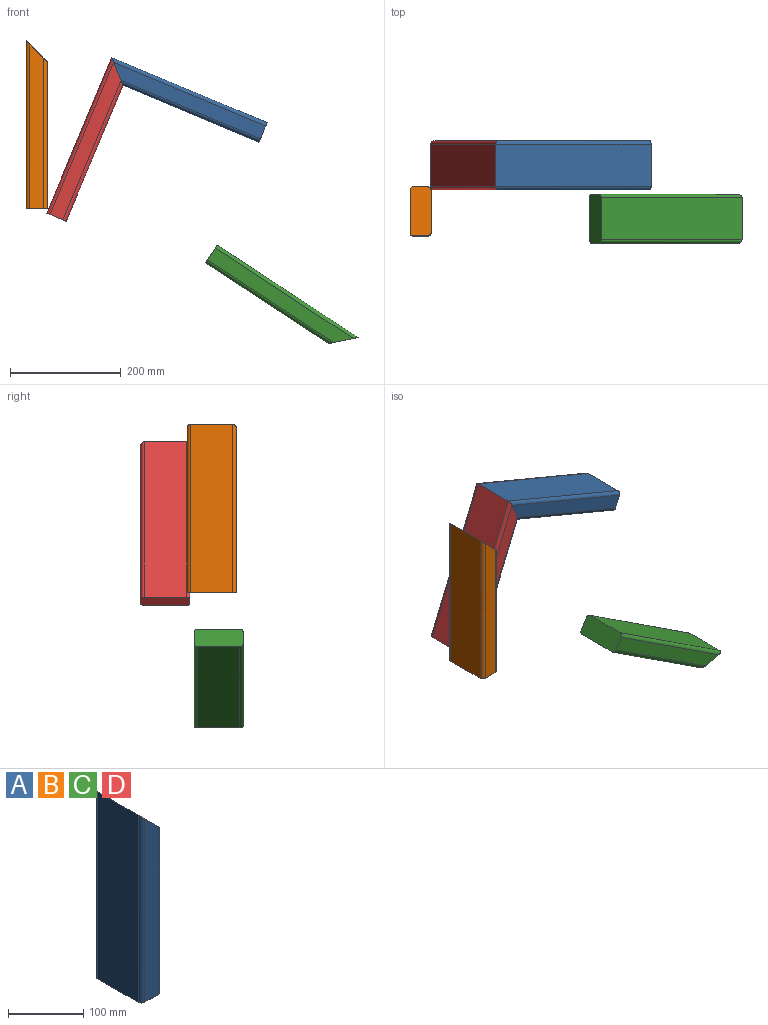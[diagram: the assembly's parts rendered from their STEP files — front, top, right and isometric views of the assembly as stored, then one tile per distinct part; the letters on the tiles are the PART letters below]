
ASSEMBLY  parts=4 mates=1
PART A: 10 faces, bbox 38.1x88.9x304.8 mm
  f0: plane 298.45x25.4mm, normal (0,-1,0), area 7258.1mm2, adj f1,f6,f8,f9
  f1: cylinder r=6.35mm len=273.05mm, axis (0,0,-1), area 2683.2mm2, adj f0,f2,f8,f9
  f2: plane 266.7x76.2mm, normal (1,0,0), area 20322.5mm2, adj f1,f3,f8,f9
  f3: cylinder r=6.35mm len=273.05mm, axis (0,0,-1), area 2683.2mm2, adj f2,f4,f8,f9
  f4: plane 298.45x25.4mm, normal (0,1,0), area 7258.1mm2, adj f3,f5,f8,f9
  f5: cylinder r=6.35mm len=304.8mm, axis (0,0,-1), area 3017.2mm2, adj f4,f7,f8,f9
  f6: cylinder r=6.35mm len=304.8mm, axis (0,0,-1), area 3017.2mm2, adj f0,f7,f8,f9
  f7: plane 304.8x76.2mm, normal (-1,0,0), area 23225.8mm2, adj f5,f6,f8,f9
  f8: plane 88.9x38.1mm, normal (0,0,-1), area 3352.5mm2, adj f0,f1,f2,f3,f4,f5,f6,f7
  f9: plane 88.9x38.1mm, normal (0.71,0,0.71), area 4741.1mm2, adj f0,f1,f2,f3,f4,f5,f6,f7
PART B: same geometry as A
PART C: same geometry as A
PART D: same geometry as A
PLACE A rot(axis=(0.55,0,-0.83),180deg) t=(612.86,192.08,273.61)mm
PLACE B at identity
PLACE C rot(axis=(0,1,0),123.3deg) t=(543.26,-12.7,40.94)mm
PLACE D rot(axis=(0,1,0),22.7deg) t=(47.43,83.7,41.53)mm
MATE fastened A.f9 <-> D.f9  axis (-0.93,0,-0.38) through (292.74,137.89,248.7)mm
